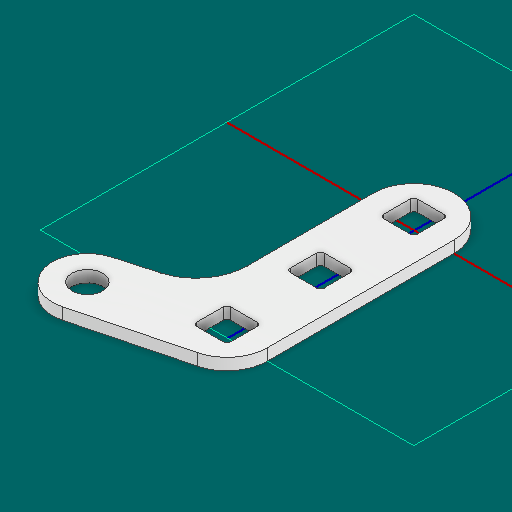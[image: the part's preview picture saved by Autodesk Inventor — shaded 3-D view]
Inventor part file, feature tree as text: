
AUTODESK INVENTOR PART (.ipt)
format: ipt  version: 2025 (Build 290162000, 162)  size: 145,408 bytes
history: native  units: in
note: dims shown in document units (in); Inventor stores cm internally (conversion verified against a paired STEP export)
features: hole x4, other x3, extrude x1, sketch x1
ambient origin geometry x8: Origin, YZ Plane, XZ Plane, XY Plane, X Axis, Y Axis, Z Axis, Center Point
bodies: Solid1 (feature_tree)
feature tree (9):
  other  "Blocks"
  extrude  "Extrusion1"  Depth=0.182in
  sketch  "Sketch1"  dims[d6=0.182in d7=0.182in d8=0.02in d9=0.5in d10=0.5in d12=0.675in d13=0.0625in d14=0.0in]
  other  "main"
  hole  "hole"  [1 undecoded]
  other  "main:1"
  hole  "hole:1"  [1 undecoded]
  hole  "hole:2"  [1 undecoded]
  hole  "hole:3"  [1 undecoded]
note: 4 required parameter values undecoded (feature->parameter linkage not recoverable at this tier; creation-order binding heuristic only, values carry confidence <= 0.55)
